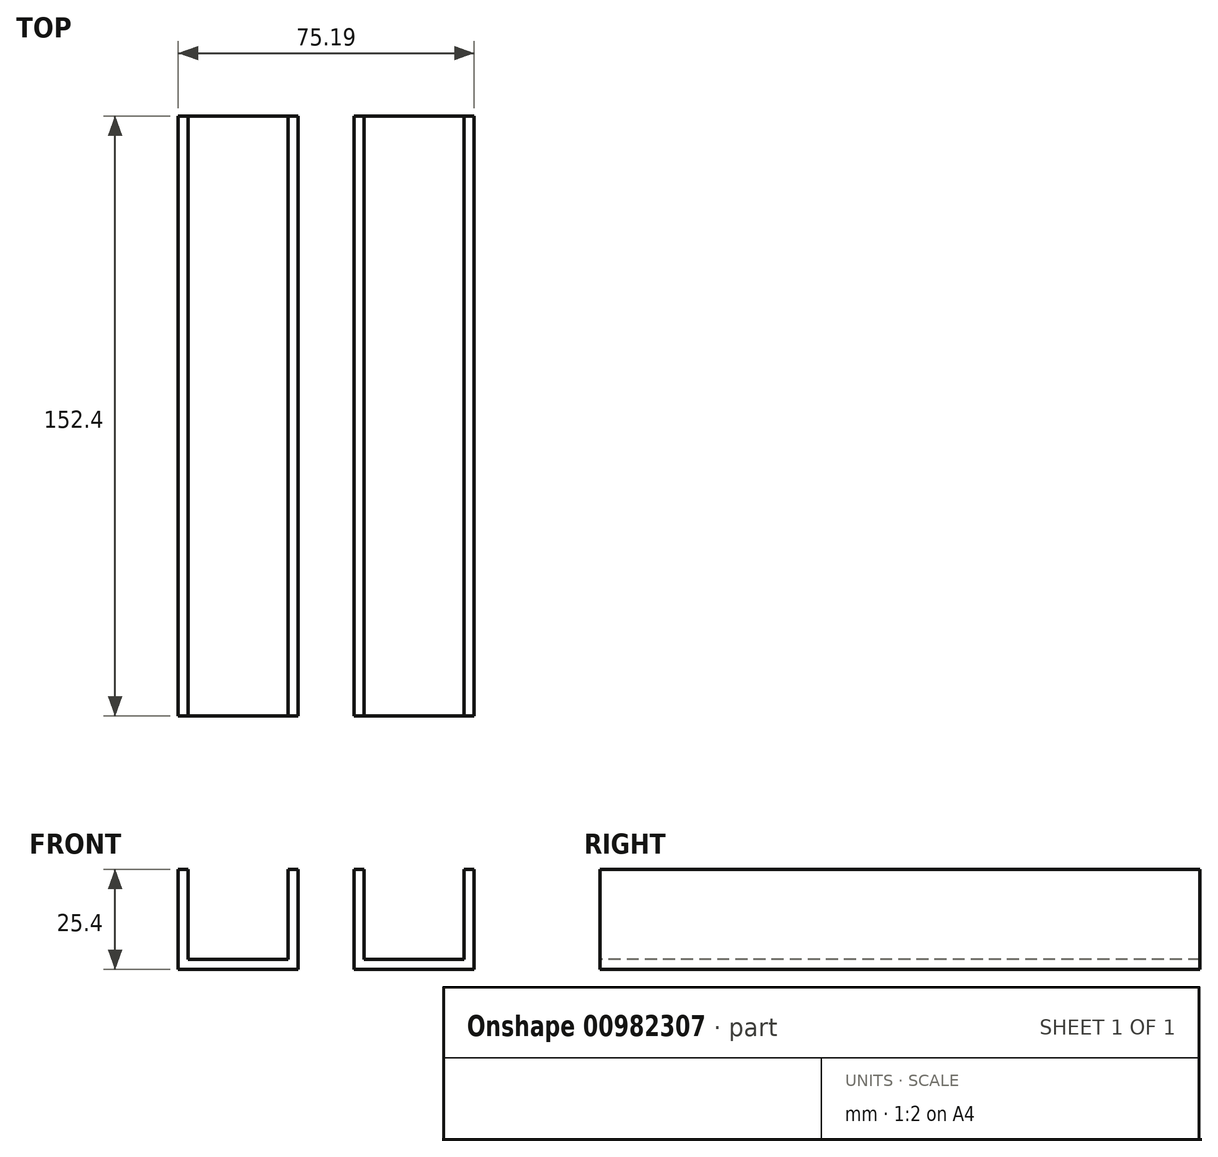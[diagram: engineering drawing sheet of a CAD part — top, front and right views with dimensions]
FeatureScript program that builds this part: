
annotation { "Feature Type Name" : "Feature", "Feature Type Description" : "" }
export const myFeature = defineFeature(function(context is Context, id is Id, definition is map)
    precondition{}
    {
        {
            var Q0;
            Q0=qCreatedBy(makeId("Top.planeOp"),FACE);
            var sketch = newSketch(context, id + "F0", { "sketchPlane" : qUnion([Q0])});
            skLineSegment(sketch, "E0.bottom", {"start": v(-37.23, 116.52) * mm, "end": v(-11.83, 116.52) * mm});
            skLineSegment(sketch, "E0.top", {"start": v(-37.23, -35.88) * mm, "end": v(-11.83, -35.88) * mm});
            skLineSegment(sketch, "E0.left", {"start": v(-37.23, 116.52) * mm, "end": v(-37.23, -35.88) * mm});
            skLineSegment(sketch, "E0.right", {"start": v(-11.83, 116.52) * mm, "end": v(-11.83, -35.88) * mm});
            skLineSegment(sketch, "E1.bottom", {"start": v(-37.23, 116.52) * mm, "end": v(-39.77, 116.52) * mm});
            skLineSegment(sketch, "E1.top", {"start": v(-37.23, -35.88) * mm, "end": v(-39.77, -35.88) * mm});
            skLineSegment(sketch, "E1.right", {"start": v(-39.77, 116.52) * mm, "end": v(-39.77, -35.88) * mm});
            skLineSegment(sketch, "E2.bottom", {"start": v(-11.83, -35.88) * mm, "end": v(-9.29, -35.88) * mm});
            skLineSegment(sketch, "E2.top", {"start": v(-11.83, 116.52) * mm, "end": v(-9.29, 116.52) * mm});
            skLineSegment(sketch, "E2.left", {"start": v(-11.83, -35.88) * mm, "end": v(-11.83, 116.52) * mm});
            skLineSegment(sketch, "E2.right", {"start": v(-9.29, -35.88) * mm, "end": v(-9.29, 116.52) * mm});
            skSolve(sketch);
        }
        {
            var Q0;
            Q0=makeQuery(id+"F0.imprint","IMPRINT",FACE,{"disambiguationData":[TD([[makeQuery(id+"F0.imprint","IMPRINT",EDGE,{"derivedFrom":sQuery(id+"F0.wireOp",EDGE,"E0.bottom")}),-1.0]])]});
            extrude(context, id + "F1", {"entities" : qUnion([Q0]), "depth" : 2.54 * mm, "offsetDistance" : 25.4 * mm});
        }
        {
            var Q0;
            Q0=makeQuery(id+"F0.imprint","IMPRINT",FACE,{"disambiguationData":[TD([[makeQuery(id+"F0.imprint","IMPRINT",EDGE,{"derivedFrom":sQuery(id+"F0.wireOp",EDGE,"E1.bottom")}),1.0]])]});
            var Q1;
            Q1=makeQuery(id+"F0.imprint","IMPRINT",FACE,{"disambiguationData":[TD([[makeQuery(id+"F0.imprint","IMPRINT",EDGE,{"derivedFrom":sQuery(id+"F0.wireOp",EDGE,"E2.bottom")}),1.0]])]});
            extrude(context, id + "F2", {"entities" : qUnion([Q0, Q1]), "operationType" : NewBodyOperationType.ADD, "depth" : 25.4 * mm, "offsetDistance" : 25.4 * mm});
        }
        {
            var Q0;
            Q0=makeQuery(id+"F1.opExtrude","SWEPT_BODY",BODY,{"disambiguationData":[OSD([sQuery(id+"F0.wireOp",EDGE,"E0.bottom"),sQuery(id+"F0.wireOp",EDGE,"E0.top"),sQuery(id+"F0.wireOp",EDGE,"E0.left"),sQuery(id+"F0.wireOp",EDGE,"E2.left")])]});
            transform(context, id + "F3", {"entities" : qUnion([Q0]), "transformType" : TransformType.TRANSLATION_3D, "dx" : 44.7 * mm, "dy" : 0 * mm, "dz" : 0 * mm, "makeCopy" : true});
        }
    });
